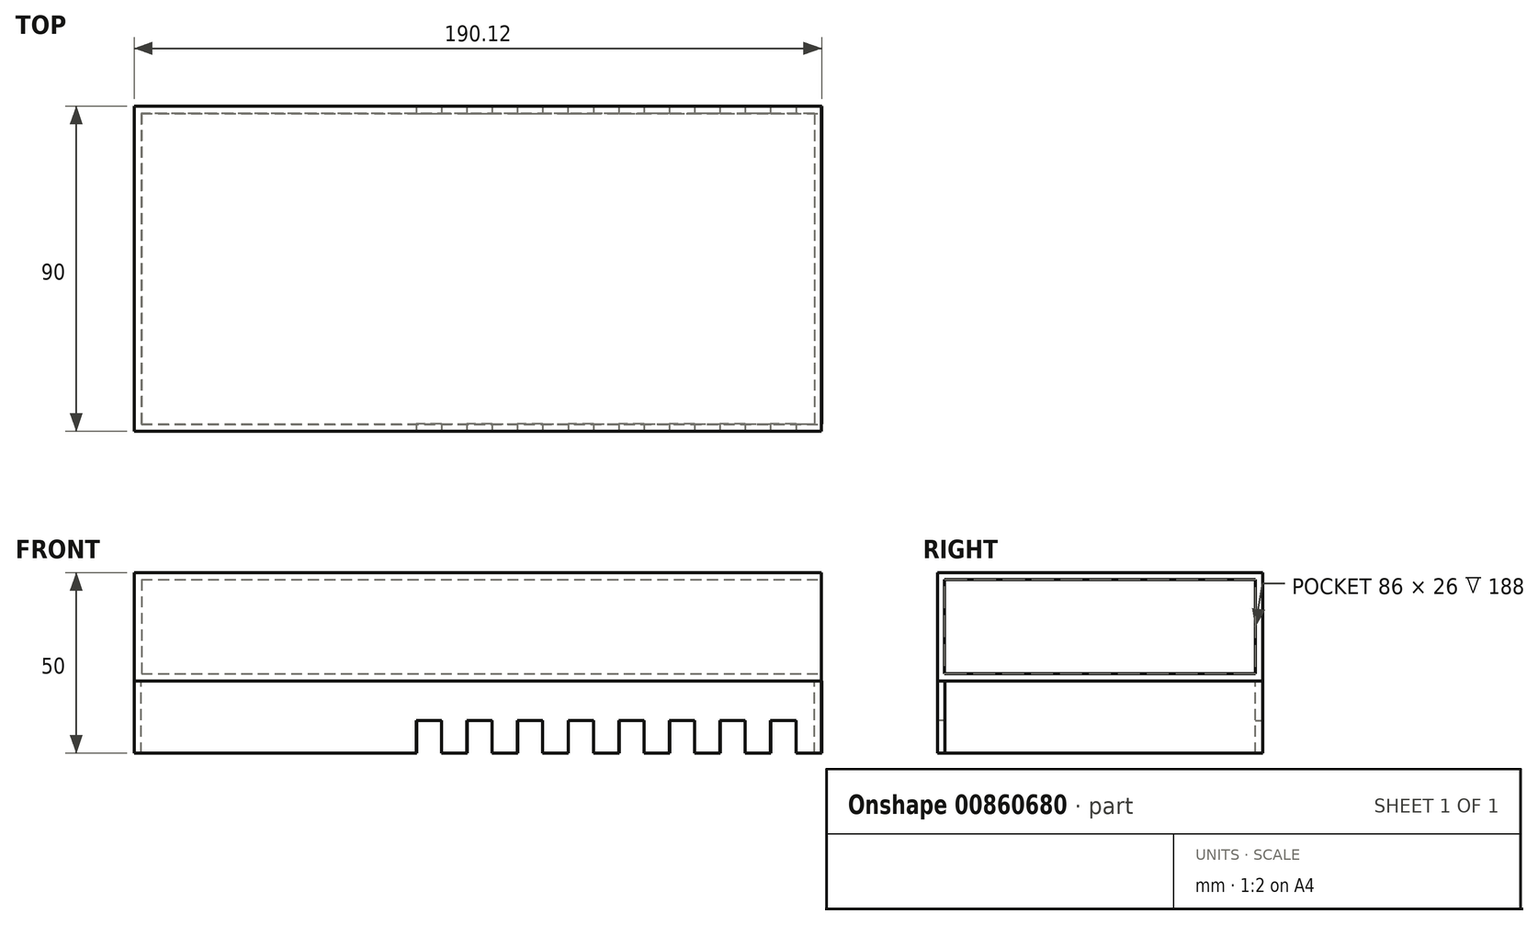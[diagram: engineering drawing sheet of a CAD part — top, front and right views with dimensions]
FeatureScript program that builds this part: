
annotation { "Feature Type Name" : "Feature", "Feature Type Description" : "" }
export const myFeature = defineFeature(function(context is Context, id is Id, definition is map)
    precondition{}
    {
        {
            var Q0;
            Q0=qCreatedBy(makeId("Top.planeOp"),FACE);
            var sketch = newSketch(context, id + "F0", { "sketchPlane" : qUnion([Q0])});
            skLineSegment(sketch, "E0.bottom", {"start": v(-95, 45) * mm, "end": v(95, 45) * mm});
            skLineSegment(sketch, "E0.top", {"start": v(-95, -45) * mm, "end": v(95, -45) * mm});
            skLineSegment(sketch, "E0.left", {"start": v(-95, 45) * mm, "end": v(-95, -45) * mm});
            skLineSegment(sketch, "E0.right", {"start": v(95, 45) * mm, "end": v(95, -45) * mm});
            skPoint(sketch, "E0.middle", {"position": v(0, 0) * mm});
            skSolve(sketch);
        }
        {
            var Q0;
            Q0=makeQuery(id+"F0.imprint","IMPRINT",FACE,{"disambiguationData":[TD([[makeQuery(id+"F0.imprint","IMPRINT",EDGE,{"derivedFrom":sQuery(id+"F0.wireOp",EDGE,"E0.bottom")}),-1.0]])]});
            extrude(context, id + "F1", {"entities" : qUnion([Q0]), "depth" : 30 * mm, "offsetDistance" : 25 * mm});
        }
        {
            var Q0;
            Q0=makeQuery(id+"F1.opExtrude","SWEPT_FACE",FACE,{"disambiguationData":[OSD([sQuery(id+"F0.wireOp",EDGE,"E0.right")])]});
            shell(context, id + "F2", {"entities" : qUnion([Q0]), "thickness" : 2 * mm});
        }
        {
            var Q0;
            Q0=qCreatedBy(makeId("Top.planeOp"),FACE);
            var sketch = newSketch(context, id + "F3", { "sketchPlane" : qUnion([Q0])});
            skLineSegment(sketch, "E1.bottom", {"start": v(95.07, 44.93) * mm, "end": v(-94.93, 44.93) * mm});
            skLineSegment(sketch, "E1.top", {"start": v(95.07, 42.93) * mm, "end": v(-94.93, 42.93) * mm});
            skLineSegment(sketch, "E1.left", {"start": v(95.07, 44.93) * mm, "end": v(95.07, 42.93) * mm});
            skLineSegment(sketch, "E1.right", {"start": v(-94.93, 44.93) * mm, "end": v(-94.93, 42.93) * mm});
            skLineSegment(sketch, "E2.top", {"start": v(94.95, -44.96) * mm, "end": v(-95.05, -44.96) * mm});
            skLineSegment(sketch, "E3", {"start": v(-95.05, -44.96) * mm, "end": v(-95.05, -42.96) * mm});
            skLineSegment(sketch, "E4", {"start": v(-95.05, -42.96) * mm, "end": v(94.96, -42.96) * mm});
            skLineSegment(sketch, "E5", {"start": v(94.96, -42.96) * mm, "end": v(94.95, -44.96) * mm});
            skLineSegment(sketch, "E6.bottom", {"start": v(-94.93, 42.93) * mm, "end": v(-95.05, 42.93) * mm});
            skLineSegment(sketch, "E6.top", {"start": v(-94.93, -42.96) * mm, "end": v(-95.05, -42.96) * mm});
            skLineSegment(sketch, "E6.left", {"start": v(-94.93, 42.93) * mm, "end": v(-94.93, -42.96) * mm});
            skLineSegment(sketch, "E6.right", {"start": v(-95.05, 42.93) * mm, "end": v(-95.05, -42.96) * mm});
            skLineSegment(sketch, "E7.bottom", {"start": v(-94.93, 42.93) * mm, "end": v(-93.05, 42.93) * mm});
            skLineSegment(sketch, "E7.top", {"start": v(-94.93, -42.96) * mm, "end": v(-93.05, -42.96) * mm});
            skLineSegment(sketch, "E7.right", {"start": v(-93.05, 42.93) * mm, "end": v(-93.05, -42.96) * mm});
            skLineSegment(sketch, "E8.bottom", {"start": v(95.07, 42.93) * mm, "end": v(93.07, 42.93) * mm});
            skLineSegment(sketch, "E8.top", {"start": v(95.07, -42.96) * mm, "end": v(93.07, -42.96) * mm});
            skLineSegment(sketch, "E8.left", {"start": v(95.07, 42.93) * mm, "end": v(95.07, -42.96) * mm});
            skLineSegment(sketch, "E8.right", {"start": v(93.07, 42.93) * mm, "end": v(93.07, -42.96) * mm});
            skSolve(sketch);
        }
        {
            var Q0;
            Q0=makeQuery(id+"F3.imprint","IMPRINT",FACE,{"disambiguationData":[TD([[makeQuery(id+"F3.imprint","IMPRINT",EDGE,{"derivedFrom":sQuery(id+"F3.wireOp",EDGE,"E1.bottom")}),1.0]])]});
            extrude(context, id + "F4", {"entities" : qUnion([Q0]), "operationType" : NewBodyOperationType.ADD, "oppositeDirection" : true, "depth" : 20 * mm, "offsetDistance" : 25 * mm});
        }
        {
            var Q0;
            Q0 = qSketchRegion(id + "F3", true);
            extrude(context, id + "F5", {"entities" : qUnion([Q0]), "operationType" : NewBodyOperationType.ADD, "oppositeDirection" : true, "depth" : 20 * mm, "offsetDistance" : 25 * mm});
        }
        {
            var Q0;
            Q0=makeQuery(id+"F4.opExtrude","SWEPT_FACE",FACE,{"disambiguationData":[OSD([sQuery(id+"F3.wireOp",EDGE,"E1.bottom")])]});
            var sketch = newSketch(context, id + "F6", { "sketchPlane" : qUnion([Q0])});
            skPoint(sketch, "E9", {"position": v(65.93, -20) * mm});
            skLineSegment(sketch, "E10.bottom", {"start": v(-81.07, -20) * mm, "end": v(-88.07, -20) * mm});
            skLineSegment(sketch, "E10.top", {"start": v(-81.07, -11) * mm, "end": v(-88.07, -11) * mm});
            skLineSegment(sketch, "E10.left", {"start": v(-81.07, -20) * mm, "end": v(-81.07, -11) * mm});
            skLineSegment(sketch, "E10.right", {"start": v(-88.07, -20) * mm, "end": v(-88.07, -11) * mm});
            skLineSegment(sketch, "E11.bottom", {"start": v(-67.07, -20) * mm, "end": v(-74.07, -20) * mm});
            skLineSegment(sketch, "E11.top", {"start": v(-67.07, -11) * mm, "end": v(-74.07, -11) * mm});
            skLineSegment(sketch, "E11.left", {"start": v(-67.07, -20) * mm, "end": v(-67.07, -11) * mm});
            skLineSegment(sketch, "E11.right", {"start": v(-74.07, -20) * mm, "end": v(-74.07, -11) * mm});
            skLineSegment(sketch, "E12.bottom", {"start": v(-53.07, -20) * mm, "end": v(-60.07, -20) * mm});
            skLineSegment(sketch, "E12.top", {"start": v(-53.07, -11) * mm, "end": v(-60.07, -11) * mm});
            skLineSegment(sketch, "E12.left", {"start": v(-53.07, -20) * mm, "end": v(-53.07, -11) * mm});
            skLineSegment(sketch, "E12.right", {"start": v(-60.07, -20) * mm, "end": v(-60.07, -11) * mm});
            skLineSegment(sketch, "E13.bottom", {"start": v(-39.07, -20) * mm, "end": v(-46.07, -20) * mm});
            skLineSegment(sketch, "E13.top", {"start": v(-39.07, -11) * mm, "end": v(-46.07, -11) * mm});
            skLineSegment(sketch, "E13.left", {"start": v(-39.07, -20) * mm, "end": v(-39.07, -11) * mm});
            skLineSegment(sketch, "E13.right", {"start": v(-46.07, -20) * mm, "end": v(-46.07, -11) * mm});
            skLineSegment(sketch, "E14.bottom", {"start": v(-25.07, -20) * mm, "end": v(-32.07, -20) * mm});
            skLineSegment(sketch, "E14.top", {"start": v(-25.07, -11) * mm, "end": v(-32.07, -11) * mm});
            skLineSegment(sketch, "E14.left", {"start": v(-25.07, -20) * mm, "end": v(-25.07, -11) * mm});
            skLineSegment(sketch, "E14.right", {"start": v(-32.07, -20) * mm, "end": v(-32.07, -11) * mm});
            skLineSegment(sketch, "E15.bottom", {"start": v(-11.07, -20) * mm, "end": v(-18.07, -20) * mm});
            skLineSegment(sketch, "E15.top", {"start": v(-11.07, -11) * mm, "end": v(-18.07, -11) * mm});
            skLineSegment(sketch, "E15.left", {"start": v(-11.07, -20) * mm, "end": v(-11.07, -11) * mm});
            skLineSegment(sketch, "E15.right", {"start": v(-18.07, -20) * mm, "end": v(-18.07, -11) * mm});
            skLineSegment(sketch, "E16.bottom", {"start": v(2.93, -20) * mm, "end": v(-4.07, -20) * mm});
            skLineSegment(sketch, "E16.top", {"start": v(2.93, -11) * mm, "end": v(-4.07, -11) * mm});
            skLineSegment(sketch, "E16.left", {"start": v(2.93, -20) * mm, "end": v(2.93, -11) * mm});
            skLineSegment(sketch, "E16.right", {"start": v(-4.07, -20) * mm, "end": v(-4.07, -11) * mm});
            skLineSegment(sketch, "E17.bottom", {"start": v(16.93, -20) * mm, "end": v(9.93, -20) * mm});
            skLineSegment(sketch, "E17.top", {"start": v(16.93, -11) * mm, "end": v(9.93, -11) * mm});
            skLineSegment(sketch, "E17.left", {"start": v(16.93, -20) * mm, "end": v(16.93, -11) * mm});
            skLineSegment(sketch, "E17.right", {"start": v(9.93, -20) * mm, "end": v(9.93, -11) * mm});
            skSolve(sketch);
        }
        {
            var Q0;
            Q0=makeQuery(id+"F6.imprint","IMPRINT",FACE,{"disambiguationData":[TD([[makeQuery(id+"F6.imprint","IMPRINT",EDGE,{"derivedFrom":sQuery(id+"F6.wireOp",EDGE,"E17.bottom")}),1.0]])]});
            var Q1;
            Q1=makeQuery(id+"F6.imprint","IMPRINT",FACE,{"disambiguationData":[TD([[makeQuery(id+"F6.imprint","IMPRINT",EDGE,{"derivedFrom":sQuery(id+"F6.wireOp",EDGE,"E16.bottom")}),1.0]])]});
            var Q2;
            Q2=makeQuery(id+"F6.imprint","IMPRINT",FACE,{"disambiguationData":[TD([[makeQuery(id+"F6.imprint","IMPRINT",EDGE,{"derivedFrom":sQuery(id+"F6.wireOp",EDGE,"E15.bottom")}),1.0]])]});
            var Q3;
            Q3=makeQuery(id+"F6.imprint","IMPRINT",FACE,{"disambiguationData":[TD([[makeQuery(id+"F6.imprint","IMPRINT",EDGE,{"derivedFrom":sQuery(id+"F6.wireOp",EDGE,"E14.bottom")}),1.0]])]});
            var Q4;
            Q4=makeQuery(id+"F6.imprint","IMPRINT",FACE,{"disambiguationData":[TD([[makeQuery(id+"F6.imprint","IMPRINT",EDGE,{"derivedFrom":sQuery(id+"F6.wireOp",EDGE,"E13.bottom")}),1.0]])]});
            var Q5;
            Q5=makeQuery(id+"F6.imprint","IMPRINT",FACE,{"disambiguationData":[TD([[makeQuery(id+"F6.imprint","IMPRINT",EDGE,{"derivedFrom":sQuery(id+"F6.wireOp",EDGE,"E12.bottom")}),1.0]])]});
            var Q6;
            Q6=makeQuery(id+"F6.imprint","IMPRINT",FACE,{"disambiguationData":[TD([[makeQuery(id+"F6.imprint","IMPRINT",EDGE,{"derivedFrom":sQuery(id+"F6.wireOp",EDGE,"E11.bottom")}),1.0]])]});
            var Q7;
            Q7=makeQuery(id+"F6.imprint","IMPRINT",FACE,{"disambiguationData":[TD([[makeQuery(id+"F6.imprint","IMPRINT",EDGE,{"derivedFrom":sQuery(id+"F6.wireOp",EDGE,"E10.bottom")}),1.0]])]});
            extrude(context, id + "F7", {"entities" : qUnion([Q0, Q1, Q2, Q3, Q4, Q5, Q6, Q7]), "operationType" : NewBodyOperationType.REMOVE, "oppositeDirection" : true, "depth" : 4 * mm, "offsetDistance" : 25 * mm});
        }
        {
            var Q0;
            Q0=makeQuery(id+"F5.opExtrude","SWEPT_FACE",FACE,{"disambiguationData":[OSD([sQuery(id+"F3.wireOp",EDGE,"E2.top")])]});
            var sketch = newSketch(context, id + "F8", { "sketchPlane" : qUnion([Q0])});
            skLineSegment(sketch, "E18.bottom", {"start": v(-10.05, -20) * mm, "end": v(-17.05, -20) * mm});
            skLineSegment(sketch, "E18.top", {"start": v(-10.05, -11) * mm, "end": v(-17.05, -11) * mm});
            skLineSegment(sketch, "E18.left", {"start": v(-10.05, -20) * mm, "end": v(-10.05, -11) * mm});
            skLineSegment(sketch, "E18.right", {"start": v(-17.05, -20) * mm, "end": v(-17.05, -11) * mm});
            skLineSegment(sketch, "E19.bottom", {"start": v(3.95, -20) * mm, "end": v(-3.05, -20) * mm});
            skLineSegment(sketch, "E19.top", {"start": v(3.95, -11) * mm, "end": v(-3.05, -11) * mm});
            skLineSegment(sketch, "E19.left", {"start": v(3.95, -20) * mm, "end": v(3.95, -11) * mm});
            skLineSegment(sketch, "E19.right", {"start": v(-3.05, -20) * mm, "end": v(-3.05, -11) * mm});
            skLineSegment(sketch, "E20.bottom", {"start": v(17.95, -20) * mm, "end": v(10.95, -20) * mm});
            skLineSegment(sketch, "E20.top", {"start": v(17.95, -11) * mm, "end": v(10.95, -11) * mm});
            skLineSegment(sketch, "E20.left", {"start": v(17.95, -20) * mm, "end": v(17.95, -11) * mm});
            skLineSegment(sketch, "E20.right", {"start": v(10.95, -20) * mm, "end": v(10.95, -11) * mm});
            skLineSegment(sketch, "E21.bottom", {"start": v(31.95, -20) * mm, "end": v(24.95, -20) * mm});
            skLineSegment(sketch, "E21.top", {"start": v(31.95, -11) * mm, "end": v(24.95, -11) * mm});
            skLineSegment(sketch, "E21.left", {"start": v(31.95, -20) * mm, "end": v(31.95, -11) * mm});
            skLineSegment(sketch, "E21.right", {"start": v(24.95, -20) * mm, "end": v(24.95, -11) * mm});
            skLineSegment(sketch, "E22.bottom", {"start": v(45.95, -20) * mm, "end": v(38.95, -20) * mm});
            skLineSegment(sketch, "E22.top", {"start": v(45.95, -11) * mm, "end": v(38.95, -11) * mm});
            skLineSegment(sketch, "E22.left", {"start": v(45.95, -20) * mm, "end": v(45.95, -11) * mm});
            skLineSegment(sketch, "E22.right", {"start": v(38.95, -20) * mm, "end": v(38.95, -11) * mm});
            skLineSegment(sketch, "E23.bottom", {"start": v(59.95, -20) * mm, "end": v(52.95, -20) * mm});
            skLineSegment(sketch, "E23.top", {"start": v(59.95, -11) * mm, "end": v(52.95, -11) * mm});
            skLineSegment(sketch, "E23.left", {"start": v(59.95, -20) * mm, "end": v(59.95, -11) * mm});
            skLineSegment(sketch, "E23.right", {"start": v(52.95, -20) * mm, "end": v(52.95, -11) * mm});
            skLineSegment(sketch, "E24.bottom", {"start": v(73.95, -20) * mm, "end": v(66.95, -20) * mm});
            skLineSegment(sketch, "E24.top", {"start": v(73.95, -11) * mm, "end": v(66.95, -11) * mm});
            skLineSegment(sketch, "E24.left", {"start": v(73.95, -20) * mm, "end": v(73.95, -11) * mm});
            skLineSegment(sketch, "E24.right", {"start": v(66.95, -20) * mm, "end": v(66.95, -11) * mm});
            skLineSegment(sketch, "E25.bottom", {"start": v(87.95, -20) * mm, "end": v(80.95, -20) * mm});
            skLineSegment(sketch, "E25.top", {"start": v(87.95, -11) * mm, "end": v(80.95, -11) * mm});
            skLineSegment(sketch, "E25.left", {"start": v(87.95, -20) * mm, "end": v(87.95, -11) * mm});
            skLineSegment(sketch, "E25.right", {"start": v(80.95, -20) * mm, "end": v(80.95, -11) * mm});
            skSolve(sketch);
        }
        {
            var Q0;
            Q0=makeQuery(id+"F8.imprint","IMPRINT",FACE,{"disambiguationData":[TD([[makeQuery(id+"F8.imprint","IMPRINT",EDGE,{"derivedFrom":sQuery(id+"F8.wireOp",EDGE,"E25.bottom")}),-1.0]])]});
            var Q1;
            Q1=makeQuery(id+"F8.imprint","IMPRINT",FACE,{"disambiguationData":[TD([[makeQuery(id+"F8.imprint","IMPRINT",EDGE,{"derivedFrom":sQuery(id+"F8.wireOp",EDGE,"E24.bottom")}),-1.0]])]});
            var Q2;
            Q2=makeQuery(id+"F8.imprint","IMPRINT",FACE,{"disambiguationData":[TD([[makeQuery(id+"F8.imprint","IMPRINT",EDGE,{"derivedFrom":sQuery(id+"F8.wireOp",EDGE,"E23.bottom")}),-1.0]])]});
            var Q3;
            Q3=makeQuery(id+"F8.imprint","IMPRINT",FACE,{"disambiguationData":[TD([[makeQuery(id+"F8.imprint","IMPRINT",EDGE,{"derivedFrom":sQuery(id+"F8.wireOp",EDGE,"E22.bottom")}),-1.0]])]});
            var Q4;
            Q4=makeQuery(id+"F8.imprint","IMPRINT",FACE,{"disambiguationData":[TD([[makeQuery(id+"F8.imprint","IMPRINT",EDGE,{"derivedFrom":sQuery(id+"F8.wireOp",EDGE,"E21.bottom")}),-1.0]])]});
            var Q5;
            Q5=makeQuery(id+"F8.imprint","IMPRINT",FACE,{"disambiguationData":[TD([[makeQuery(id+"F8.imprint","IMPRINT",EDGE,{"derivedFrom":sQuery(id+"F8.wireOp",EDGE,"E20.bottom")}),-1.0]])]});
            var Q6;
            Q6=makeQuery(id+"F8.imprint","IMPRINT",FACE,{"disambiguationData":[TD([[makeQuery(id+"F8.imprint","IMPRINT",EDGE,{"derivedFrom":sQuery(id+"F8.wireOp",EDGE,"E19.bottom")}),-1.0]])]});
            var Q7;
            Q7=makeQuery(id+"F8.imprint","IMPRINT",FACE,{"disambiguationData":[TD([[makeQuery(id+"F8.imprint","IMPRINT",EDGE,{"derivedFrom":sQuery(id+"F8.wireOp",EDGE,"E18.bottom")}),-1.0]])]});
            extrude(context, id + "F9", {"entities" : qUnion([Q0, Q1, Q2, Q3, Q4, Q5, Q6, Q7]), "operationType" : NewBodyOperationType.REMOVE, "oppositeDirection" : true, "depth" : 4 * mm, "offsetDistance" : 25 * mm});
        }
    });
